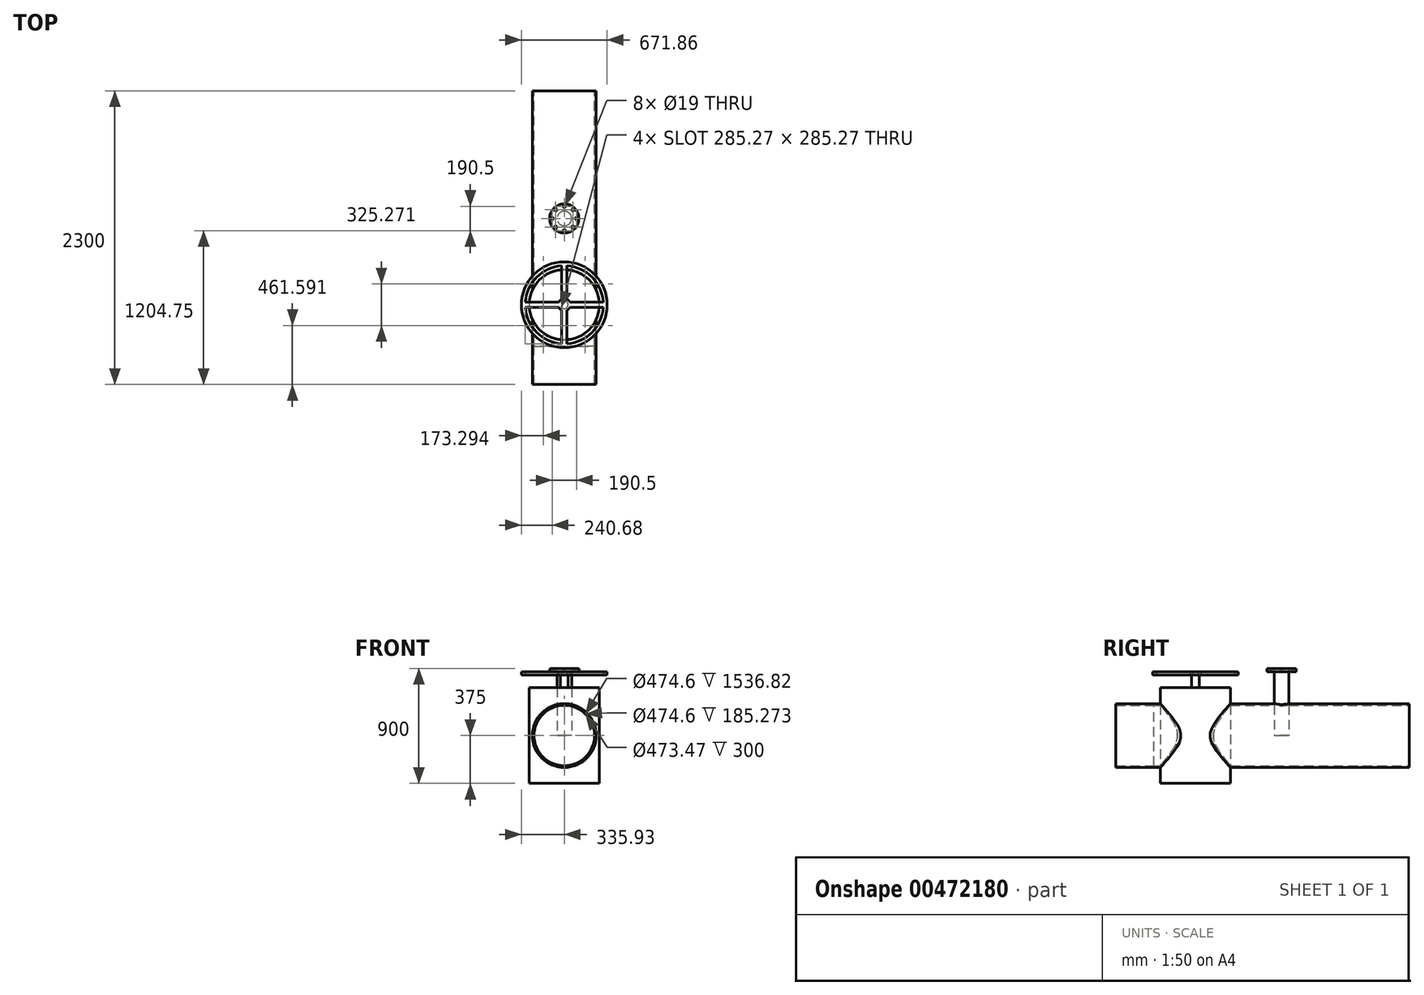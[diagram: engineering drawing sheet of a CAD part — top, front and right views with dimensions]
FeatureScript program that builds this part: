
annotation { "Feature Type Name" : "Feature", "Feature Type Description" : "" }
export const myFeature = defineFeature(function(context is Context, id is Id, definition is map)
    precondition{}
    {
        {
            var Q0;
            Q0=qCreatedBy(makeId("Front.planeOp"),FACE);
            var sketch = newSketch(context, id + "F0", { "sketchPlane" : qUnion([Q0])});
            skCircle(sketch, "E0", {"center": v(0, 0) * mm, "radius": 250 * mm});
            skCircle(sketch, "E1", {"center": v(0, 0) * mm, "radius": 237.3 * mm});
            skSolve(sketch);
        }
        {
            var Q0;
            Q0 = qSketchRegion(id + "F0", true);
            extrude(context, id + "F1", {"entities" : qUnion([Q0]), "depth" : 2000 * mm});
        }
        {
            var Q0;
            Q0=qCreatedBy(makeId("Top.planeOp"),FACE);
            var sketch = newSketch(context, id + "F2", { "sketchPlane" : qUnion([Q0])});
            skCircle(sketch, "E2", {"center": v(0, -1000) * mm, "radius": 57 * mm});
            skSolve(sketch);
        }
        {
            var Q0;
            Q0 = qSketchRegion(id + "F2", true);
            extrude(context, id + "F3", {"entities" : qUnion([Q0]), "operationType" : NewBodyOperationType.ADD, "depth" : 500 * mm});
        }
        {
            var Q0;
            Q0=makeQuery(id+"F3.opExtrude","CAP_FACE",FACE,{"disambiguationData":[OSD([sQuery(id+"F2.wireOp",EDGE,"E2")])],"isStart":false});
            var sketch = newSketch(context, id + "F4", { "sketchPlane" : qUnion([Q0])});
            skCircle(sketch, "E3", {"center": v(0, -1000) * mm, "radius": 114.3 * mm});
            skSolve(sketch);
        }
        {
            var Q0;
            Q0 = qSketchRegion(id + "F4", true);
            extrude(context, id + "F5", {"entities" : qUnion([Q0]), "operationType" : NewBodyOperationType.ADD, "depth" : 25 * mm});
        }
        {
            var Q0;
            Q0=makeQuery(id+"F5.opExtrude","CAP_FACE",FACE,{"disambiguationData":[OSD([sQuery(id+"F4.wireOp",EDGE,"E3")])],"isStart":false});
            var sketch = newSketch(context, id + "F6", { "sketchPlane" : qUnion([Q0])});
            skCircle(sketch, "E4", {"center": v(0, -904.75) * mm, "radius": 9.5 * mm});
            skLineSegment(sketch, "E5", {"start": v(0, -1000) * mm, "end": v(0, -904.75) * mm, "construction": true});
            skCircle(sketch, "E6.1.0", {"center": v(-67.35, -932.65) * mm, "radius": 9.5 * mm});
            skCircle(sketch, "E6.2.0", {"center": v(-95.25, -1000) * mm, "radius": 9.5 * mm});
            skCircle(sketch, "E6.3.0", {"center": v(-67.35, -1067.35) * mm, "radius": 9.5 * mm});
            skCircle(sketch, "E6.4.0", {"center": v(0, -1095.25) * mm, "radius": 9.5 * mm});
            skCircle(sketch, "E6.5.0", {"center": v(67.35, -1067.35) * mm, "radius": 9.5 * mm});
            skCircle(sketch, "E6.6.0", {"center": v(95.25, -1000) * mm, "radius": 9.5 * mm});
            skCircle(sketch, "E6.7.0", {"center": v(67.35, -932.65) * mm, "radius": 9.5 * mm});
            skPoint(sketch, "E6.center", {"position": v(0, -1000) * mm});
            skSolve(sketch);
        }
        {
            var Q0;
            Q0 = qSketchRegion(id + "F6", true);
            extrude(context, id + "F7", {"entities" : qUnion([Q0]), "operationType" : NewBodyOperationType.REMOVE, "oppositeDirection" : true, "depth" : 30 * mm});
        }
        {
            var Q0;
            Q0=makeQuery(id+"F1.opExtrude","CAP_FACE",FACE,{"disambiguationData":[OSD([sQuery(id+"F0.wireOp",EDGE,"E0"),sQuery(id+"F0.wireOp",EDGE,"E1")])],"isStart":false});
            var sketch = newSketch(context, id + "F8", { "sketchPlane" : qUnion([Q0])});
            skCircle(sketch, "E7", {"center": v(0, 0) * mm, "radius": 250 * mm});
            skCircle(sketch, "E8", {"center": v(0, 0) * mm, "radius": 236.74 * mm});
            skSolve(sketch);
        }
        {
            var Q0;
            Q0 = qSketchRegion(id + "F8", true);
            extrude(context, id + "F9", {"entities" : qUnion([Q0]), "operationType" : NewBodyOperationType.ADD, "depth" : 300 * mm});
        }
        {
            var Q0;
            Q0=qCreatedBy(makeId("Top.planeOp"),FACE);
            var sketch = newSketch(context, id + "F10", { "sketchPlane" : qUnion([Q0])});
            skCircle(sketch, "E9", {"center": v(0, -1675.77) * mm, "radius": 275 * mm});
            skSolve(sketch);
        }
        {
            var Q0;
            Q0 = qSketchRegion(id + "F10", true);
            extrude(context, id + "F11", {"entities" : qUnion([Q0]), "operationType" : NewBodyOperationType.ADD, "endBound" : BoundingType.SYMMETRIC, "depth" : 750 * mm});
        }
        {
            var Q0;
            Q0=makeQuery(id+"F11.opExtrude","CAP_FACE",FACE,{"disambiguationData":[OSD([sQuery(id+"F10.wireOp",EDGE,"E9")])],"isStart":false});
            var sketch = newSketch(context, id + "F12", { "sketchPlane" : qUnion([Q0])});
            skCircle(sketch, "E10", {"center": v(0, -1675.77) * mm, "radius": 30 * mm});
            skSolve(sketch);
        }
        {
            var Q0;
            Q0 = qSketchRegion(id + "F12", true);
            extrude(context, id + "F13", {"entities" : qUnion([Q0]), "operationType" : NewBodyOperationType.ADD, "depth" : 100 * mm});
        }
        {
            var Q0;
            Q0=makeQuery(id+"F13.opExtrude","CAP_FACE",FACE,{"disambiguationData":[OSD([sQuery(id+"F12.wireOp",EDGE,"E10")])],"isStart":false});
            var sketch = newSketch(context, id + "F14", { "sketchPlane" : qUnion([Q0])});
            skArc(sketch, "E11", {"start": v(20, -1718.86) * mm, "mid": v(33.59, -1709.36) * mm, "end": v(43.08, -1695.77) * mm});
            skArc(sketch, "E12", {"start": v(20, -1981.04) * mm, "mid": v(216.32, -1892.1) * mm, "end": v(305.27, -1695.77) * mm});
            skCircle(sketch, "E13", {"center": v(0, -1675.77) * mm, "radius": 335.93 * mm});
            skLineSegment(sketch, "E14", {"start": v(43.08, -1695.77) * mm, "end": v(305.27, -1695.77) * mm});
            skLineSegment(sketch, "E15", {"start": v(43.08, -1655.77) * mm, "end": v(305.27, -1655.77) * mm});
            skLineSegment(sketch, "E16", {"start": v(-43.08, -1695.77) * mm, "end": v(-305.27, -1695.77) * mm});
            skLineSegment(sketch, "E17", {"start": v(-43.08, -1655.77) * mm, "end": v(-305.27, -1655.77) * mm});
            skLineSegment(sketch, "E18", {"start": v(-20, -1718.86) * mm, "end": v(-20, -1981.04) * mm});
            skLineSegment(sketch, "E19", {"start": v(20, -1718.86) * mm, "end": v(20, -1981.04) * mm});
            skLineSegment(sketch, "E20", {"start": v(-20, -1632.69) * mm, "end": v(-20, -1370.5) * mm});
            skLineSegment(sketch, "E21", {"start": v(20, -1632.69) * mm, "end": v(20, -1370.5) * mm});
            skArc(sketch, "E22.trimOffspring", {"start": v(-20, -1632.69) * mm, "mid": v(-33.59, -1642.19) * mm, "end": v(-43.08, -1655.77) * mm});
            skArc(sketch, "E23.trimOffspring", {"start": v(-43.08, -1695.77) * mm, "mid": v(-33.59, -1709.36) * mm, "end": v(-20, -1718.86) * mm});
            skArc(sketch, "E24.trimOffspring", {"start": v(43.08, -1655.77) * mm, "mid": v(33.59, -1642.19) * mm, "end": v(20, -1632.69) * mm});
            skArc(sketch, "E25.trimOffspring", {"start": v(305.27, -1655.77) * mm, "mid": v(216.32, -1459.45) * mm, "end": v(20, -1370.5) * mm});
            skArc(sketch, "E26.trimOffspring", {"start": v(-20, -1370.5) * mm, "mid": v(-216.32, -1459.45) * mm, "end": v(-305.27, -1655.77) * mm});
            skArc(sketch, "E27.trimOffspring", {"start": v(-305.27, -1695.77) * mm, "mid": v(-216.32, -1892.1) * mm, "end": v(-20, -1981.04) * mm});
            skSolve(sketch);
        }
        {
            var Q0;
            Q0 = qSketchRegion(id + "F14", true);
            extrude(context, id + "F15", {"entities" : qUnion([Q0]), "operationType" : NewBodyOperationType.ADD, "depth" : 25 * mm});
        }
    });
